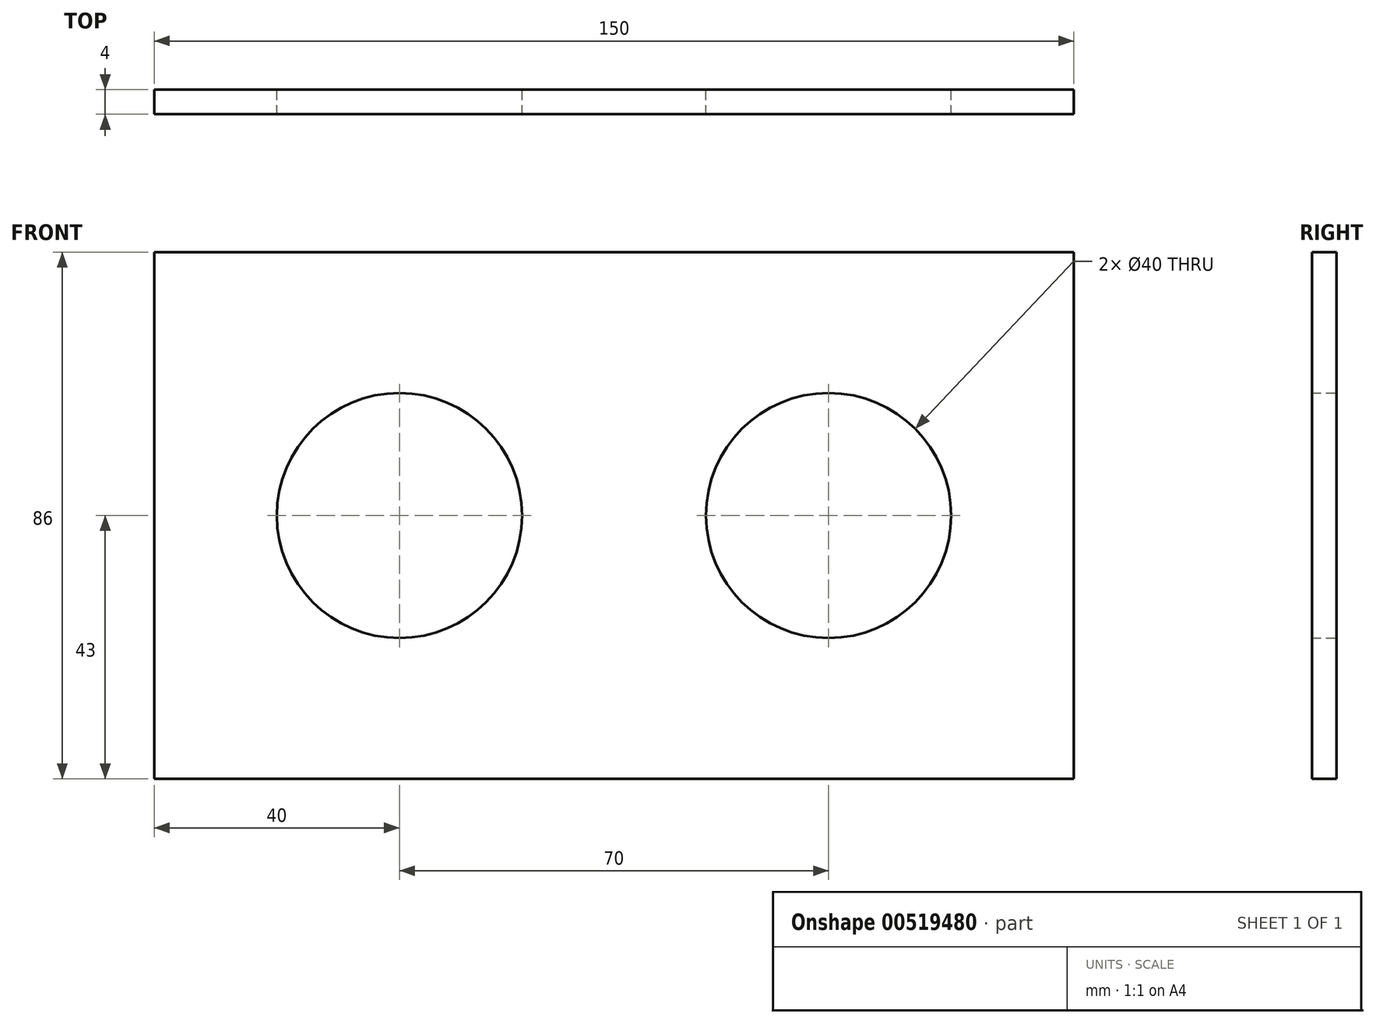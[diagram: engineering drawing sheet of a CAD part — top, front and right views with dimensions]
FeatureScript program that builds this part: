
annotation { "Feature Type Name" : "Feature", "Feature Type Description" : "" }
export const myFeature = defineFeature(function(context is Context, id is Id, definition is map)
    precondition{}
    {
        {
            var Q0;
            Q0=qCreatedBy(makeId("Front.planeOp"),FACE);
            var sketch = newSketch(context, id + "F0", { "sketchPlane" : qUnion([Q0])});
            skLineSegment(sketch, "E0", {"start": v(0, 0) * mm, "end": v(150, 0) * mm});
            skLineSegment(sketch, "E1", {"start": v(150, 0) * mm, "end": v(150, 86) * mm});
            skLineSegment(sketch, "E2", {"start": v(0, 86) * mm, "end": v(0, 0) * mm});
            skLineSegment(sketch, "E3", {"start": v(0, 86) * mm, "end": v(150, 86) * mm});
            skCircle(sketch, "E4", {"center": v(110, 43) * mm, "radius": 20 * mm});
            skCircle(sketch, "E5", {"center": v(40, 43) * mm, "radius": 20 * mm});
            skPoint(sketch, "E6", {"position": v(150, 43) * mm});
            skPoint(sketch, "E7", {"position": v(0, 43) * mm});
            skSolve(sketch);
        }
        {
            var Q0;
            Q0=makeQuery(id+"F0.imprint","IMPRINT",FACE,{"disambiguationData":[TD([[makeQuery(id+"F0.imprint","IMPRINT",EDGE,{"derivedFrom":sQuery(id+"F0.wireOp",EDGE,"E0")}),1.0]])]});
            extrude(context, id + "F1", {"entities" : qUnion([Q0]), "depth" : 4 * mm, "offsetDistance" : 25 * mm});
        }
    });
